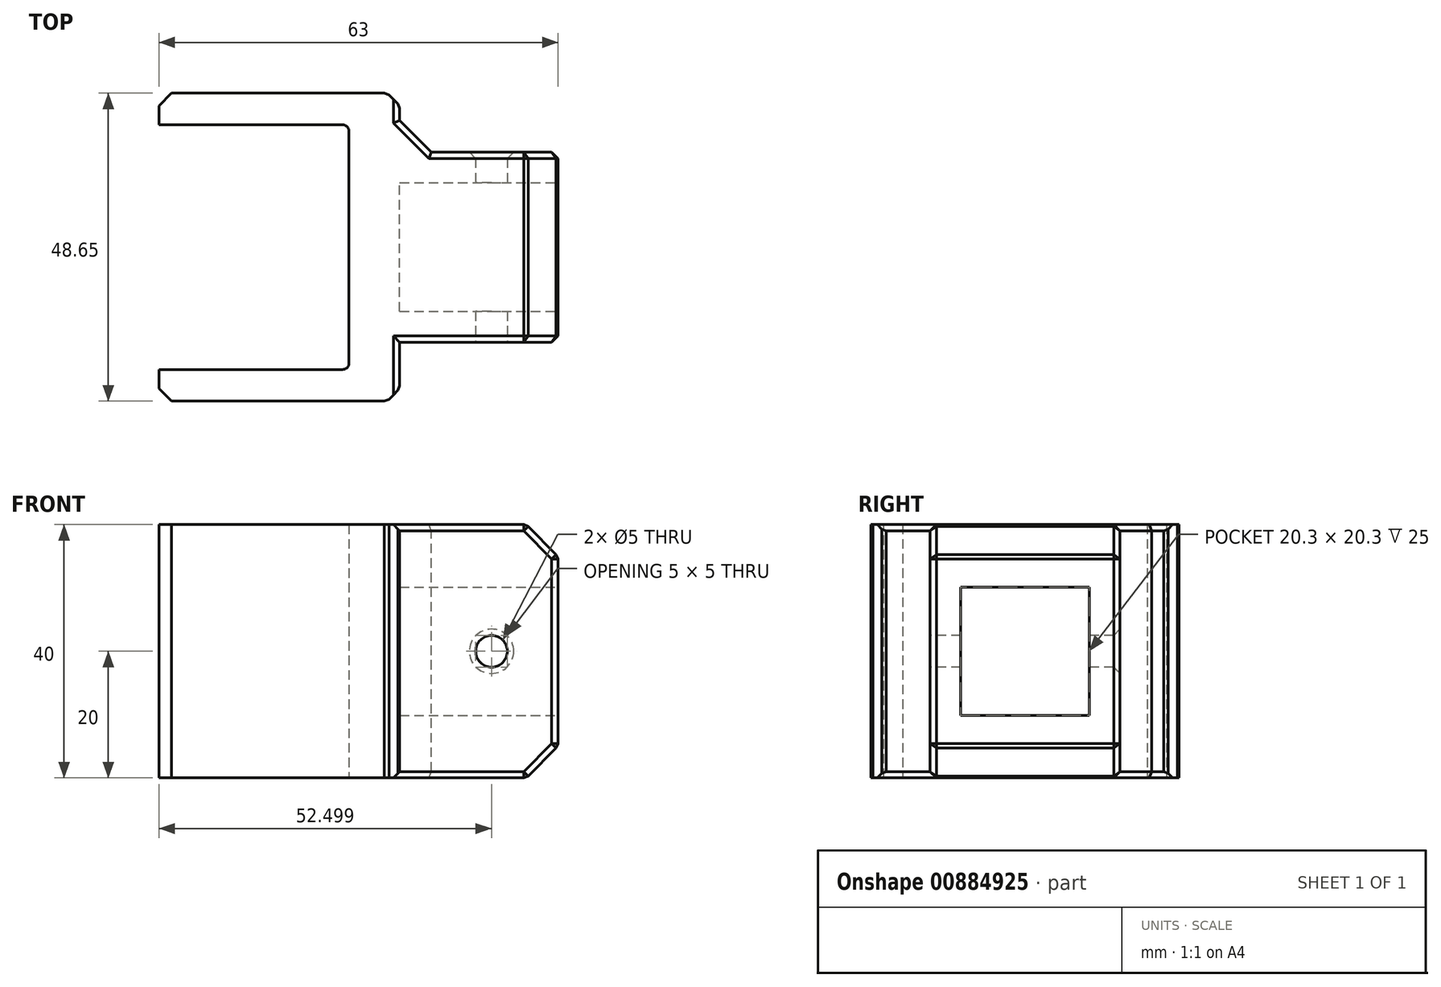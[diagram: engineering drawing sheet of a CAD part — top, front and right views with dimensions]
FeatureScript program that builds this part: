
annotation { "Feature Type Name" : "Feature", "Feature Type Description" : "" }
export const myFeature = defineFeature(function(context is Context, id is Id, definition is map)
    precondition{}
    {
        {
            var Q0;
            Q0=qCreatedBy(makeId("Top.planeOp"),FACE);
            var sketch = newSketch(context, id + "F0", { "sketchPlane" : qUnion([Q0])});
            skLineSegment(sketch, "E0.top", {"start": v(-72.12, -48.29) * mm, "end": v(-110.12, -48.29) * mm});
            skLineSegment(sketch, "E0.right", {"start": v(-110.12, -43.29) * mm, "end": v(-110.12, -48.29) * mm});
            skLineSegment(sketch, "E1.top", {"start": v(-72.12, 0.36) * mm, "end": v(-110.12, 0.36) * mm});
            skLineSegment(sketch, "E1.right", {"start": v(-110.12, -4.64) * mm, "end": v(-110.12, 0.36) * mm});
            skPoint(sketch, "E2", {"position": v(-72.12, 0.36) * mm});
            skLineSegment(sketch, "E3", {"start": v(-72.12, 0.36) * mm, "end": v(-72.12, -48.29) * mm});
            skPoint(sketch, "E4.visualSharp", {"position": v(-47.12, 0.36) * mm});
            skPoint(sketch, "E5.visualSharp", {"position": v(-47.12, -48.29) * mm});
            skPoint(sketch, "E6.end.orphan", {"position": v(-80.12, 0.36) * mm});
            skLineSegment(sketch, "E7.trimOffspring", {"start": v(-80.12, -43.29) * mm, "end": v(-110.12, -43.29) * mm});
            skLineSegment(sketch, "E8.trimOffspring", {"start": v(-80.12, -4.64) * mm, "end": v(-110.12, -4.64) * mm});
            skPoint(sketch, "E0.left.start.orphan", {"position": v(-47.12, -43.29) * mm});
            skPoint(sketch, "E1.left.start.orphan", {"position": v(-47.12, -4.64) * mm});
            skLineSegment(sketch, "E9", {"start": v(-47.12, -8.97) * mm, "end": v(-47.12, -38.97) * mm});
            skLineSegment(sketch, "E10", {"start": v(-80.12, 0.36) * mm, "end": v(-80.12, -48.29) * mm});
            skLineSegment(sketch, "E11.bottom", {"start": v(-47.12, -8.97) * mm, "end": v(-47.12, -8.97) * mm});
            skLineSegment(sketch, "E11.top", {"start": v(-47.12, -38.97) * mm, "end": v(-47.12, -38.97) * mm});
            skPoint(sketch, "E11.middle", {"position": v(-47.12, -23.97) * mm});
            skLineSegment(sketch, "E12", {"start": v(-47.12, -8.97) * mm, "end": v(-72.12, -8.97) * mm});
            skLineSegment(sketch, "E13", {"start": v(-47.12, -38.97) * mm, "end": v(-72.12, -38.97) * mm});
            skSolve(sketch);
        }
        {
            var Q0;
            Q0=makeQuery(id+"F0.imprint","IMPRINT",FACE,{"disambiguationData":[TD([[makeQuery(id+"F0.imprint","IMPRINT",EDGE,{"derivedFrom":sQuery(id+"F0.wireOp",EDGE,"tIqOB3Vk-ss04-YIaf-baA0-UyKqDhGvaing.left")}),1.0]])]});
            var Q1;
            {var subQ4=sQuery(id+"F0.wireOp",EDGE,"E3");Q1=makeQuery(id+"F0.imprint","IMPRINT",FACE,{"disambiguationData":[TD([[makeQuery(id+"F0.imprint","IMPRINT",EDGE,{"derivedFrom":subQ4}),-1.0]])]});}
            var Q2;
            {var subQ0=sQuery(id+"F0.wireOp",EDGE,"E1.right");Q2=makeQuery(id+"F0.imprint","IMPRINT",FACE,{"disambiguationData":[TD([[makeQuery(id+"F0.imprint","IMPRINT",EDGE,{"derivedFrom":subQ0}),-1.0]])]});}
            var Q3;
            {var subQ0=sQuery(id+"F0.wireOp",EDGE,"E0.right");Q3=makeQuery(id+"F0.imprint","IMPRINT",FACE,{"disambiguationData":[TD([[makeQuery(id+"F0.imprint","IMPRINT",EDGE,{"derivedFrom":subQ0}),1.0]])]});}
            extrude(context, id + "F1", {"entities" : qUnion([Q0, Q1, Q2, Q3]), "depth" : 40 * mm, "offsetDistance" : 25 * mm});
        }
        {
            var Q0;
            Q0=makeQuery(id+"F0.imprint","IMPRINT",FACE,{"disambiguationData":[TD([[makeQuery(id+"F0.imprint","IMPRINT",EDGE,{"derivedFrom":sQuery(id+"F0.wireOp",EDGE,"tIqOB3Vk-ss04-YIaf-baA0-UyKqDhGvaing.right")}),-1.0]])]});
            var Q1;
            Q1=makeQuery(id+"F0.imprint","IMPRINT",FACE,{"disambiguationData":[TD([[makeQuery(id+"F0.imprint","IMPRINT",EDGE,{"derivedFrom":sQuery(id+"F0.wireOp",EDGE,"E3")}),1.0]])]});
            extrude(context, id + "F2", {"entities" : qUnion([Q0, Q1]), "operationType" : NewBodyOperationType.ADD, "depth" : 40 * mm, "offsetDistance" : 25 * mm});
        }
        {
            var Q0;
            Q0=makeQuery(id+"F2.opExtrude","SWEPT_FACE",FACE,{"disambiguationData":[OSD([sQuery(id+"F0.wireOp",EDGE,"E9")])]});
            var sketch = newSketch(context, id + "F3", { "sketchPlane" : qUnion([Q0])});
            skLineSegment(sketch, "E14.bottom", {"start": v(-34.12, 9.85) * mm, "end": v(-13.82, 9.85) * mm});
            skLineSegment(sketch, "E14.top", {"start": v(-34.12, 30.15) * mm, "end": v(-13.82, 30.15) * mm});
            skLineSegment(sketch, "E14.left", {"start": v(-34.12, 9.85) * mm, "end": v(-34.12, 30.15) * mm});
            skLineSegment(sketch, "E14.right", {"start": v(-13.82, 9.85) * mm, "end": v(-13.82, 30.15) * mm});
            skPoint(sketch, "E14.middle", {"position": v(-23.97, 20) * mm});
            skPoint(sketch, "E14.middle.positionSnap0", {"position": v(-8.97, 20) * mm});
            skPoint(sketch, "E14.middle.positionSnap1", {"position": v(-23.97, 0) * mm});
            skPoint(sketch, "E14.centerSnap0", {"position": v(-8.97, 20) * mm});
            skPoint(sketch, "E14.centerSnap1", {"position": v(-23.97, 0) * mm});
            skSolve(sketch);
        }
        {
            var Q0;
            Q0=makeQuery(id+"F3.imprint","IMPRINT",FACE,{"disambiguationData":[TD([[makeQuery(id+"F3.imprint","IMPRINT",EDGE,{"derivedFrom":sQuery(id+"F3.wireOp",EDGE,"E14.bottom")}),1.0]])]});
            extrude(context, id + "F4", {"entities" : qUnion([Q0]), "operationType" : NewBodyOperationType.REMOVE, "oppositeDirection" : true, "depth" : 25 * mm, "offsetDistance" : 25 * mm});
        }
        {
            var Q0;
            Q0=makeQuery(id+"F2.opExtrude","SWEPT_EDGE",EDGE,{"disambiguationData":[OSD([sQuery(id+"F0.wireOp",EDGE,"E3"),sQuery(id+"F0.wireOp",EDGE,"E13")])]});
            var Q1;
            Q1=makeQuery(id+"F2.opExtrude","SWEPT_EDGE",EDGE,{"disambiguationData":[OSD([sQuery(id+"F0.wireOp",EDGE,"E3"),sQuery(id+"F0.wireOp",EDGE,"E12")])]});
            var Q2;
            Q2=makeQuery(id+"F2.opExtrude","CAP_EDGE",EDGE,{"disambiguationData":[OSD([sQuery(id+"F0.wireOp",EDGE,"E9")])],"isStart":true});
            var Q3;
            Q3=makeQuery(id+"F2.opExtrude","CAP_EDGE",EDGE,{"disambiguationData":[OSD([sQuery(id+"F0.wireOp",EDGE,"E9")])],"isStart":false});
            chamfer(context, id + "F5", {"entities" : qUnion([Q0, Q1, Q2, Q3]), "width" : 5 * mm, "tangentPropagation" : true});
        }
        {
            var Q0;
            Q0=makeQuery(id+"F1.opExtrude","SWEPT_EDGE",EDGE,{"disambiguationData":[OSD([sQuery(id+"F0.wireOp",EDGE,"E0.top"),sQuery(id+"F0.wireOp",EDGE,"E0.right")])]});
            var Q1;
            Q1=makeQuery(id+"F1.opExtrude","SWEPT_EDGE",EDGE,{"disambiguationData":[OSD([sQuery(id+"F0.wireOp",EDGE,"E1.top"),sQuery(id+"F0.wireOp",EDGE,"E1.right")])]});
            var Q2;
            Q2=makeQuery(id+"F1.opExtrude","SWEPT_EDGE",EDGE,{"disambiguationData":[OSD([sQuery(id+"F0.wireOp",EDGE,"E0.top"),sQuery(id+"F0.wireOp",EDGE,"E3")])]});
            var Q3;
            Q3=makeQuery(id+"F1.opExtrude","SWEPT_EDGE",EDGE,{"disambiguationData":[OSD([sQuery(id+"F0.wireOp",EDGE,"E1.top"),sQuery(id+"F0.wireOp",EDGE,"E3")])]});
            chamfer(context, id + "F6", {"entities" : qUnion([Q0, Q1, Q2, Q3]), "width" : 2 * mm, "tangentPropagation" : true});
        }
        {
            var Q0;
            Q0=makeQuery(id+"F1.opExtrude","SWEPT_EDGE",EDGE,{"disambiguationData":[OSD([sQuery(id+"F0.wireOp",EDGE,"E7.trimOffspring"),sQuery(id+"F0.wireOp",EDGE,"E10")])]});
            var Q1;
            Q1=makeQuery(id+"F1.opExtrude","SWEPT_EDGE",EDGE,{"disambiguationData":[OSD([sQuery(id+"F0.wireOp",EDGE,"E8.trimOffspring"),sQuery(id+"F0.wireOp",EDGE,"E10")])]});
            fillet(context, id + "F7", {"entities" : qUnion([Q0, Q1]), "radius" : 1 * mm, "tangentPropagation" : true, "allowEdgeOverflow" : false});
        }
        {
            var Q0;
            {var subQ0=sQuery(id+"F0.wireOp",EDGE,"E12");var subQ1=sQuery(id+"F0.wireOp",EDGE,"E3");Q0=makeQuery(id+"F5.opChamfer","BLEND_EDGE",EDGE,{"blendedFrom":[makeQuery(id+"F2.opExtrude","SWEPT_EDGE",EDGE,{"disambiguationData":[OSD([subQ1,subQ0])]}),makeQuery(id+"F2.boolean.opBoolean","MERGE",FACE,{"derivedFrom":[makeQuery(id+"F1.opExtrude","CAP_FACE",FACE,{"disambiguationData":[OSD([sQuery(id+"F0.wireOp",EDGE,"E0.top"),sQuery(id+"F0.wireOp",EDGE,"E0.right"),sQuery(id+"F0.wireOp",EDGE,"E1.top"),sQuery(id+"F0.wireOp",EDGE,"E1.right"),subQ1,sQuery(id+"F0.wireOp",EDGE,"E7.trimOffspring"),sQuery(id+"F0.wireOp",EDGE,"E8.trimOffspring"),sQuery(id+"F0.wireOp",EDGE,"E10")])],"isStart":false}),makeQuery(id+"F2.opExtrude","CAP_FACE",FACE,{"disambiguationData":[OSD([subQ1,sQuery(id+"F0.wireOp",EDGE,"E9"),subQ0,sQuery(id+"F0.wireOp",EDGE,"E13")])],"isStart":false})]})],"blendedInto":[makeQuery(id+"F2.boolean.opBoolean","MERGE",FACE,{"derivedFrom":[makeQuery(id+"F1.opExtrude","CAP_FACE",FACE,{"disambiguationData":[OSD([sQuery(id+"F0.wireOp",EDGE,"E0.top"),sQuery(id+"F0.wireOp",EDGE,"E0.right"),sQuery(id+"F0.wireOp",EDGE,"E1.top"),sQuery(id+"F0.wireOp",EDGE,"E1.right"),subQ1,sQuery(id+"F0.wireOp",EDGE,"E7.trimOffspring"),sQuery(id+"F0.wireOp",EDGE,"E8.trimOffspring"),sQuery(id+"F0.wireOp",EDGE,"E10")])],"isStart":false}),makeQuery(id+"F2.opExtrude","CAP_FACE",FACE,{"disambiguationData":[OSD([subQ1,sQuery(id+"F0.wireOp",EDGE,"E9"),subQ0,sQuery(id+"F0.wireOp",EDGE,"E13")])],"isStart":false})]})]});}
            var Q1;
            Q1=makeQuery(id+"F2.opExtrude","CAP_EDGE",EDGE,{"disambiguationData":[OSD([sQuery(id+"F0.wireOp",EDGE,"E12")])],"isStart":false});
            var Q2;
            {var subQ0=sQuery(id+"F0.wireOp",EDGE,"E13");var subQ1=sQuery(id+"F0.wireOp",EDGE,"E3");Q2=makeQuery(id+"F5.opChamfer","BLEND_EDGE",EDGE,{"blendedFrom":[makeQuery(id+"F2.opExtrude","SWEPT_EDGE",EDGE,{"disambiguationData":[OSD([subQ1,subQ0])]}),makeQuery(id+"F2.boolean.opBoolean","MERGE",FACE,{"derivedFrom":[makeQuery(id+"F1.opExtrude","CAP_FACE",FACE,{"disambiguationData":[OSD([sQuery(id+"F0.wireOp",EDGE,"E0.top"),sQuery(id+"F0.wireOp",EDGE,"E0.right"),sQuery(id+"F0.wireOp",EDGE,"E1.top"),sQuery(id+"F0.wireOp",EDGE,"E1.right"),subQ1,sQuery(id+"F0.wireOp",EDGE,"E7.trimOffspring"),sQuery(id+"F0.wireOp",EDGE,"E8.trimOffspring"),sQuery(id+"F0.wireOp",EDGE,"E10")])],"isStart":false}),makeQuery(id+"F2.opExtrude","CAP_FACE",FACE,{"disambiguationData":[OSD([subQ1,sQuery(id+"F0.wireOp",EDGE,"E9"),sQuery(id+"F0.wireOp",EDGE,"E12"),subQ0])],"isStart":false})]})],"blendedInto":[makeQuery(id+"F2.boolean.opBoolean","MERGE",FACE,{"derivedFrom":[makeQuery(id+"F1.opExtrude","CAP_FACE",FACE,{"disambiguationData":[OSD([sQuery(id+"F0.wireOp",EDGE,"E0.top"),sQuery(id+"F0.wireOp",EDGE,"E0.right"),sQuery(id+"F0.wireOp",EDGE,"E1.top"),sQuery(id+"F0.wireOp",EDGE,"E1.right"),subQ1,sQuery(id+"F0.wireOp",EDGE,"E7.trimOffspring"),sQuery(id+"F0.wireOp",EDGE,"E8.trimOffspring"),sQuery(id+"F0.wireOp",EDGE,"E10")])],"isStart":false}),makeQuery(id+"F2.opExtrude","CAP_FACE",FACE,{"disambiguationData":[OSD([subQ1,sQuery(id+"F0.wireOp",EDGE,"E9"),sQuery(id+"F0.wireOp",EDGE,"E12"),subQ0])],"isStart":false})]})]});}
            var Q3;
            Q3=makeQuery(id+"F2.opExtrude","CAP_EDGE",EDGE,{"disambiguationData":[OSD([sQuery(id+"F0.wireOp",EDGE,"E13")])],"isStart":false});
            var Q4;
            {var subQ0=sQuery(id+"F0.wireOp",EDGE,"E13");var subQ1=sQuery(id+"F0.wireOp",EDGE,"E3");Q4=makeQuery(id+"F5.opChamfer","BLEND_EDGE",EDGE,{"blendedFrom":[makeQuery(id+"F2.opExtrude","SWEPT_EDGE",EDGE,{"disambiguationData":[OSD([subQ1,subQ0])]}),makeQuery(id+"F2.boolean.opBoolean","MERGE",FACE,{"derivedFrom":[makeQuery(id+"F1.opExtrude","CAP_FACE",FACE,{"disambiguationData":[OSD([sQuery(id+"F0.wireOp",EDGE,"E0.top"),sQuery(id+"F0.wireOp",EDGE,"E0.right"),sQuery(id+"F0.wireOp",EDGE,"E1.top"),sQuery(id+"F0.wireOp",EDGE,"E1.right"),subQ1,sQuery(id+"F0.wireOp",EDGE,"E7.trimOffspring"),sQuery(id+"F0.wireOp",EDGE,"E8.trimOffspring"),sQuery(id+"F0.wireOp",EDGE,"E10")])],"isStart":true}),makeQuery(id+"F2.opExtrude","CAP_FACE",FACE,{"disambiguationData":[OSD([subQ1,sQuery(id+"F0.wireOp",EDGE,"E9"),sQuery(id+"F0.wireOp",EDGE,"E12"),subQ0])],"isStart":true})]})],"blendedInto":[makeQuery(id+"F2.boolean.opBoolean","MERGE",FACE,{"derivedFrom":[makeQuery(id+"F1.opExtrude","CAP_FACE",FACE,{"disambiguationData":[OSD([sQuery(id+"F0.wireOp",EDGE,"E0.top"),sQuery(id+"F0.wireOp",EDGE,"E0.right"),sQuery(id+"F0.wireOp",EDGE,"E1.top"),sQuery(id+"F0.wireOp",EDGE,"E1.right"),subQ1,sQuery(id+"F0.wireOp",EDGE,"E7.trimOffspring"),sQuery(id+"F0.wireOp",EDGE,"E8.trimOffspring"),sQuery(id+"F0.wireOp",EDGE,"E10")])],"isStart":true}),makeQuery(id+"F2.opExtrude","CAP_FACE",FACE,{"disambiguationData":[OSD([subQ1,sQuery(id+"F0.wireOp",EDGE,"E9"),sQuery(id+"F0.wireOp",EDGE,"E12"),subQ0])],"isStart":true})]})]});}
            var Q5;
            Q5=makeQuery(id+"F2.opExtrude","CAP_EDGE",EDGE,{"disambiguationData":[OSD([sQuery(id+"F0.wireOp",EDGE,"E13")])],"isStart":true});
            var Q6;
            {var subQ0=sQuery(id+"F0.wireOp",EDGE,"E12");var subQ1=sQuery(id+"F0.wireOp",EDGE,"E3");Q6=makeQuery(id+"F5.opChamfer","BLEND_EDGE",EDGE,{"blendedFrom":[makeQuery(id+"F2.opExtrude","SWEPT_EDGE",EDGE,{"disambiguationData":[OSD([subQ1,subQ0])]}),makeQuery(id+"F2.boolean.opBoolean","MERGE",FACE,{"derivedFrom":[makeQuery(id+"F1.opExtrude","CAP_FACE",FACE,{"disambiguationData":[OSD([sQuery(id+"F0.wireOp",EDGE,"E0.top"),sQuery(id+"F0.wireOp",EDGE,"E0.right"),sQuery(id+"F0.wireOp",EDGE,"E1.top"),sQuery(id+"F0.wireOp",EDGE,"E1.right"),subQ1,sQuery(id+"F0.wireOp",EDGE,"E7.trimOffspring"),sQuery(id+"F0.wireOp",EDGE,"E8.trimOffspring"),sQuery(id+"F0.wireOp",EDGE,"E10")])],"isStart":true}),makeQuery(id+"F2.opExtrude","CAP_FACE",FACE,{"disambiguationData":[OSD([subQ1,sQuery(id+"F0.wireOp",EDGE,"E9"),subQ0,sQuery(id+"F0.wireOp",EDGE,"E13")])],"isStart":true})]})],"blendedInto":[makeQuery(id+"F2.boolean.opBoolean","MERGE",FACE,{"derivedFrom":[makeQuery(id+"F1.opExtrude","CAP_FACE",FACE,{"disambiguationData":[OSD([sQuery(id+"F0.wireOp",EDGE,"E0.top"),sQuery(id+"F0.wireOp",EDGE,"E0.right"),sQuery(id+"F0.wireOp",EDGE,"E1.top"),sQuery(id+"F0.wireOp",EDGE,"E1.right"),subQ1,sQuery(id+"F0.wireOp",EDGE,"E7.trimOffspring"),sQuery(id+"F0.wireOp",EDGE,"E8.trimOffspring"),sQuery(id+"F0.wireOp",EDGE,"E10")])],"isStart":true}),makeQuery(id+"F2.opExtrude","CAP_FACE",FACE,{"disambiguationData":[OSD([subQ1,sQuery(id+"F0.wireOp",EDGE,"E9"),subQ0,sQuery(id+"F0.wireOp",EDGE,"E13")])],"isStart":true})]})]});}
            var Q7;
            Q7=makeQuery(id+"F2.opExtrude","CAP_EDGE",EDGE,{"disambiguationData":[OSD([sQuery(id+"F0.wireOp",EDGE,"E12")])],"isStart":true});
            var Q8;
            Q8=makeQuery(id+"F5.opChamfer","BLEND_EDGE",EDGE,{"blendedFrom":[makeQuery(id+"F2.opExtrude","CAP_EDGE",EDGE,{"disambiguationData":[OSD([sQuery(id+"F0.wireOp",EDGE,"E9")])],"isStart":true}),makeQuery(id+"F2.opExtrude","SWEPT_FACE",FACE,{"disambiguationData":[OSD([sQuery(id+"F0.wireOp",EDGE,"E13")])]})],"blendedInto":[makeQuery(id+"F2.opExtrude","SWEPT_FACE",FACE,{"disambiguationData":[OSD([sQuery(id+"F0.wireOp",EDGE,"E13")])]})]});
            var Q9;
            Q9=makeQuery(id+"F5.opChamfer","BLEND_EDGE",EDGE,{"blendedFrom":[makeQuery(id+"F2.opExtrude","CAP_EDGE",EDGE,{"disambiguationData":[OSD([sQuery(id+"F0.wireOp",EDGE,"E9")])],"isStart":false}),makeQuery(id+"F2.opExtrude","SWEPT_FACE",FACE,{"disambiguationData":[OSD([sQuery(id+"F0.wireOp",EDGE,"E13")])]})],"blendedInto":[makeQuery(id+"F2.opExtrude","SWEPT_FACE",FACE,{"disambiguationData":[OSD([sQuery(id+"F0.wireOp",EDGE,"E13")])]})]});
            var Q10;
            Q10=makeQuery(id+"F2.opExtrude","SWEPT_EDGE",EDGE,{"disambiguationData":[OSD([sQuery(id+"F0.wireOp",EDGE,"E9"),sQuery(id+"F0.wireOp",EDGE,"E13")])]});
            var Q11;
            Q11=makeQuery(id+"F2.opExtrude","SWEPT_EDGE",EDGE,{"disambiguationData":[OSD([sQuery(id+"F0.wireOp",EDGE,"E9"),sQuery(id+"F0.wireOp",EDGE,"E12")])]});
            var Q12;
            Q12=makeQuery(id+"F5.opChamfer","BLEND_EDGE",EDGE,{"blendedFrom":[makeQuery(id+"F2.opExtrude","CAP_EDGE",EDGE,{"disambiguationData":[OSD([sQuery(id+"F0.wireOp",EDGE,"E9")])],"isStart":false}),makeQuery(id+"F2.opExtrude","SWEPT_FACE",FACE,{"disambiguationData":[OSD([sQuery(id+"F0.wireOp",EDGE,"E12")])]})],"blendedInto":[makeQuery(id+"F2.opExtrude","SWEPT_FACE",FACE,{"disambiguationData":[OSD([sQuery(id+"F0.wireOp",EDGE,"E12")])]})]});
            var Q13;
            Q13=makeQuery(id+"F5.opChamfer","BLEND_EDGE",EDGE,{"blendedFrom":[makeQuery(id+"F2.opExtrude","CAP_EDGE",EDGE,{"disambiguationData":[OSD([sQuery(id+"F0.wireOp",EDGE,"E9")])],"isStart":true}),makeQuery(id+"F2.opExtrude","SWEPT_FACE",FACE,{"disambiguationData":[OSD([sQuery(id+"F0.wireOp",EDGE,"E12")])]})],"blendedInto":[makeQuery(id+"F2.opExtrude","SWEPT_FACE",FACE,{"disambiguationData":[OSD([sQuery(id+"F0.wireOp",EDGE,"E12")])]})]});
            var Q14;
            {var subQ0=sQuery(id+"F0.wireOp",EDGE,"E9");var subQ1=sQuery(id+"F0.wireOp",EDGE,"E3");Q14=makeQuery(id+"F5.opChamfer","BLEND_EDGE",EDGE,{"blendedFrom":[makeQuery(id+"F2.opExtrude","CAP_EDGE",EDGE,{"disambiguationData":[OSD([subQ0])],"isStart":true}),makeQuery(id+"F2.boolean.opBoolean","MERGE",FACE,{"derivedFrom":[makeQuery(id+"F1.opExtrude","CAP_FACE",FACE,{"disambiguationData":[OSD([sQuery(id+"F0.wireOp",EDGE,"E0.top"),sQuery(id+"F0.wireOp",EDGE,"E0.right"),sQuery(id+"F0.wireOp",EDGE,"E1.top"),sQuery(id+"F0.wireOp",EDGE,"E1.right"),subQ1,sQuery(id+"F0.wireOp",EDGE,"E7.trimOffspring"),sQuery(id+"F0.wireOp",EDGE,"E8.trimOffspring"),sQuery(id+"F0.wireOp",EDGE,"E10")])],"isStart":true}),makeQuery(id+"F2.opExtrude","CAP_FACE",FACE,{"disambiguationData":[OSD([subQ1,subQ0,sQuery(id+"F0.wireOp",EDGE,"E12"),sQuery(id+"F0.wireOp",EDGE,"E13")])],"isStart":true})]})],"blendedInto":[makeQuery(id+"F2.boolean.opBoolean","MERGE",FACE,{"derivedFrom":[makeQuery(id+"F1.opExtrude","CAP_FACE",FACE,{"disambiguationData":[OSD([sQuery(id+"F0.wireOp",EDGE,"E0.top"),sQuery(id+"F0.wireOp",EDGE,"E0.right"),sQuery(id+"F0.wireOp",EDGE,"E1.top"),sQuery(id+"F0.wireOp",EDGE,"E1.right"),subQ1,sQuery(id+"F0.wireOp",EDGE,"E7.trimOffspring"),sQuery(id+"F0.wireOp",EDGE,"E8.trimOffspring"),sQuery(id+"F0.wireOp",EDGE,"E10")])],"isStart":true}),makeQuery(id+"F2.opExtrude","CAP_FACE",FACE,{"disambiguationData":[OSD([subQ1,subQ0,sQuery(id+"F0.wireOp",EDGE,"E12"),sQuery(id+"F0.wireOp",EDGE,"E13")])],"isStart":true})]})]});}
            var Q15;
            {var subQ0=sQuery(id+"F0.wireOp",EDGE,"E9");var subQ1=sQuery(id+"F0.wireOp",EDGE,"E3");Q15=makeQuery(id+"F5.opChamfer","BLEND_EDGE",EDGE,{"blendedFrom":[makeQuery(id+"F2.opExtrude","CAP_EDGE",EDGE,{"disambiguationData":[OSD([subQ0])],"isStart":false}),makeQuery(id+"F2.boolean.opBoolean","MERGE",FACE,{"derivedFrom":[makeQuery(id+"F1.opExtrude","CAP_FACE",FACE,{"disambiguationData":[OSD([sQuery(id+"F0.wireOp",EDGE,"E0.top"),sQuery(id+"F0.wireOp",EDGE,"E0.right"),sQuery(id+"F0.wireOp",EDGE,"E1.top"),sQuery(id+"F0.wireOp",EDGE,"E1.right"),subQ1,sQuery(id+"F0.wireOp",EDGE,"E7.trimOffspring"),sQuery(id+"F0.wireOp",EDGE,"E8.trimOffspring"),sQuery(id+"F0.wireOp",EDGE,"E10")])],"isStart":false}),makeQuery(id+"F2.opExtrude","CAP_FACE",FACE,{"disambiguationData":[OSD([subQ1,subQ0,sQuery(id+"F0.wireOp",EDGE,"E12"),sQuery(id+"F0.wireOp",EDGE,"E13")])],"isStart":false})]})],"blendedInto":[makeQuery(id+"F2.boolean.opBoolean","MERGE",FACE,{"derivedFrom":[makeQuery(id+"F1.opExtrude","CAP_FACE",FACE,{"disambiguationData":[OSD([sQuery(id+"F0.wireOp",EDGE,"E0.top"),sQuery(id+"F0.wireOp",EDGE,"E0.right"),sQuery(id+"F0.wireOp",EDGE,"E1.top"),sQuery(id+"F0.wireOp",EDGE,"E1.right"),subQ1,sQuery(id+"F0.wireOp",EDGE,"E7.trimOffspring"),sQuery(id+"F0.wireOp",EDGE,"E8.trimOffspring"),sQuery(id+"F0.wireOp",EDGE,"E10")])],"isStart":false}),makeQuery(id+"F2.opExtrude","CAP_FACE",FACE,{"disambiguationData":[OSD([subQ1,subQ0,sQuery(id+"F0.wireOp",EDGE,"E12"),sQuery(id+"F0.wireOp",EDGE,"E13")])],"isStart":false})]})]});}
            var Q16;
            {var subQ0=sQuery(id+"F0.wireOp",EDGE,"E9");Q16=makeQuery(id+"F5.opChamfer","BLEND_EDGE",EDGE,{"blendedFrom":[makeQuery(id+"F2.opExtrude","CAP_EDGE",EDGE,{"disambiguationData":[OSD([subQ0])],"isStart":false}),makeQuery(id+"F2.opExtrude","SWEPT_FACE",FACE,{"disambiguationData":[OSD([subQ0])]})],"blendedInto":[makeQuery(id+"F2.opExtrude","SWEPT_FACE",FACE,{"disambiguationData":[OSD([subQ0])]})]});}
            var Q17;
            {var subQ0=sQuery(id+"F0.wireOp",EDGE,"E9");Q17=makeQuery(id+"F5.opChamfer","BLEND_EDGE",EDGE,{"blendedFrom":[makeQuery(id+"F2.opExtrude","CAP_EDGE",EDGE,{"disambiguationData":[OSD([subQ0])],"isStart":true}),makeQuery(id+"F2.opExtrude","SWEPT_FACE",FACE,{"disambiguationData":[OSD([subQ0])]})],"blendedInto":[makeQuery(id+"F2.opExtrude","SWEPT_FACE",FACE,{"disambiguationData":[OSD([subQ0])]})]});}
            var Q18;
            {var subQ1=sQuery(id+"F0.wireOp",EDGE,"E3");var subQ2=sQuery(id+"F0.wireOp",EDGE,"E0.top");Q18=makeQuery(id+"F2.boolean.opBoolean","SPLIT",EDGE,{"disambiguationData":[TD([makeQuery(id+"F1.opExtrude","SWEPT_FACE",FACE,{"disambiguationData":[OSD([subQ2])]})])],"derivedFrom":makeQuery(id+"F1.opExtrude","CAP_EDGE",EDGE,{"disambiguationData":[OSD([subQ1])],"isStart":false})});}
            var Q19;
            {var subQ1=sQuery(id+"F0.wireOp",EDGE,"E3");var subQ2=sQuery(id+"F0.wireOp",EDGE,"E0.top");Q19=makeQuery(id+"F2.boolean.opBoolean","SPLIT",EDGE,{"disambiguationData":[TD([makeQuery(id+"F1.opExtrude","SWEPT_FACE",FACE,{"disambiguationData":[OSD([subQ2])]})])],"derivedFrom":makeQuery(id+"F1.opExtrude","CAP_EDGE",EDGE,{"disambiguationData":[OSD([subQ1])],"isStart":true})});}
            var Q20;
            {var subQ1=sQuery(id+"F0.wireOp",EDGE,"E3");var subQ2=sQuery(id+"F0.wireOp",EDGE,"E1.top");Q20=makeQuery(id+"F2.boolean.opBoolean","SPLIT",EDGE,{"disambiguationData":[TD([makeQuery(id+"F1.opExtrude","SWEPT_FACE",FACE,{"disambiguationData":[OSD([subQ2])]})])],"derivedFrom":makeQuery(id+"F1.opExtrude","CAP_EDGE",EDGE,{"disambiguationData":[OSD([subQ1])],"isStart":false})});}
            var Q21;
            {var subQ1=sQuery(id+"F0.wireOp",EDGE,"E3");var subQ2=sQuery(id+"F0.wireOp",EDGE,"E1.top");Q21=makeQuery(id+"F2.boolean.opBoolean","SPLIT",EDGE,{"disambiguationData":[TD([makeQuery(id+"F1.opExtrude","SWEPT_FACE",FACE,{"disambiguationData":[OSD([subQ2])]})])],"derivedFrom":makeQuery(id+"F1.opExtrude","CAP_EDGE",EDGE,{"disambiguationData":[OSD([subQ1])],"isStart":true})});}
            var Q22;
            {var subQ3=sQuery(id+"F0.wireOp",EDGE,"E3");var subQ10=sQuery(id+"F0.wireOp",EDGE,"E0.top");Q22=makeQuery(id+"F6.opChamfer","BLEND_EDGE",EDGE,{"blendedFrom":[makeQuery(id+"F1.opExtrude","SWEPT_EDGE",EDGE,{"disambiguationData":[OSD([subQ10,subQ3])]}),makeQuery(id+"F2.boolean.opBoolean","SPLIT",FACE,{"disambiguationData":[TD([makeQuery(id+"F1.opExtrude","SWEPT_FACE",FACE,{"disambiguationData":[OSD([subQ10])]})])],"derivedFrom":makeQuery(id+"F1.opExtrude","SWEPT_FACE",FACE,{"disambiguationData":[OSD([subQ3])]})})],"blendedInto":[makeQuery(id+"F2.boolean.opBoolean","SPLIT",FACE,{"disambiguationData":[TD([makeQuery(id+"F1.opExtrude","SWEPT_FACE",FACE,{"disambiguationData":[OSD([subQ10])]})])],"derivedFrom":makeQuery(id+"F1.opExtrude","SWEPT_FACE",FACE,{"disambiguationData":[OSD([subQ3])]})})]});}
            var Q23;
            {var subQ0=sQuery(id+"F0.wireOp",EDGE,"E1.top");var subQ4=sQuery(id+"F0.wireOp",EDGE,"E3");Q23=makeQuery(id+"F6.opChamfer","BLEND_EDGE",EDGE,{"blendedFrom":[makeQuery(id+"F1.opExtrude","SWEPT_EDGE",EDGE,{"disambiguationData":[OSD([subQ0,subQ4])]}),makeQuery(id+"F2.boolean.opBoolean","SPLIT",FACE,{"disambiguationData":[TD([makeQuery(id+"F1.opExtrude","SWEPT_FACE",FACE,{"disambiguationData":[OSD([subQ0])]})])],"derivedFrom":makeQuery(id+"F1.opExtrude","SWEPT_FACE",FACE,{"disambiguationData":[OSD([subQ4])]})})],"blendedInto":[makeQuery(id+"F2.boolean.opBoolean","SPLIT",FACE,{"disambiguationData":[TD([makeQuery(id+"F1.opExtrude","SWEPT_FACE",FACE,{"disambiguationData":[OSD([subQ0])]})])],"derivedFrom":makeQuery(id+"F1.opExtrude","SWEPT_FACE",FACE,{"disambiguationData":[OSD([subQ4])]})})]});}
            var Q24;
            {var subQ0=sQuery(id+"F0.wireOp",EDGE,"E1.top");Q24=makeQuery(id+"F6.opChamfer","BLEND_EDGE",EDGE,{"blendedFrom":[makeQuery(id+"F1.opExtrude","SWEPT_EDGE",EDGE,{"disambiguationData":[OSD([subQ0,sQuery(id+"F0.wireOp",EDGE,"E3")])]}),makeQuery(id+"F1.opExtrude","SWEPT_FACE",FACE,{"disambiguationData":[OSD([subQ0])]})],"blendedInto":[makeQuery(id+"F1.opExtrude","SWEPT_FACE",FACE,{"disambiguationData":[OSD([subQ0])]})]});}
            var Q25;
            {var subQ0=sQuery(id+"F0.wireOp",EDGE,"E0.top");Q25=makeQuery(id+"F6.opChamfer","BLEND_EDGE",EDGE,{"blendedFrom":[makeQuery(id+"F1.opExtrude","SWEPT_EDGE",EDGE,{"disambiguationData":[OSD([subQ0,sQuery(id+"F0.wireOp",EDGE,"E3")])]}),makeQuery(id+"F1.opExtrude","SWEPT_FACE",FACE,{"disambiguationData":[OSD([subQ0])]})],"blendedInto":[makeQuery(id+"F1.opExtrude","SWEPT_FACE",FACE,{"disambiguationData":[OSD([subQ0])]})]});}
            chamfer(context, id + "F8", {"entities" : qUnion([Q0, Q1, Q2, Q3, Q4, Q5, Q6, Q7, Q8, Q9, Q10, Q11, Q12, Q13, Q14, Q15, Q16, Q17, Q18, Q19, Q20, Q21, Q22, Q23, Q24, Q25]), "width" : 1 * mm, "tangentPropagation" : true});
        }
        {
            var Q0;
            Q0=makeQuery(id+"F2.opExtrude","SWEPT_FACE",FACE,{"disambiguationData":[OSD([sQuery(id+"F0.wireOp",EDGE,"E13")])]});
            var sketch = newSketch(context, id + "F9", { "sketchPlane" : qUnion([Q0])});
            skLineSegment(sketch, "E15", {"start": v(-67.12, 20) * mm, "end": v(-48.12, 20) * mm});
            skCircle(sketch, "E16", {"center": v(-57.62, 20) * mm, "radius": 2.5 * mm});
            skSolve(sketch);
        }
        {
            var Q0;
            {var subQ0=sQuery(id+"F9.wireOp",EDGE,"E16");var subQ1=sQuery(id+"F9.wireOp",EDGE,"E15");var subQ2=makeQuery(id+"F9.imprint","INTERSECT",VERTEX,{"disambiguationData":[OD(0.0)],"derivedFrom":[subQ1,subQ0]});Q0=makeQuery(id+"F9.imprint","IMPRINT",FACE,{"disambiguationData":[TD([[makeQuery(id+"F9.imprint","IMPRINT",EDGE,{"disambiguationData":[TD([[subQ2,-1.0]])],"derivedFrom":subQ1}),1.0]])]});}
            var Q1;
            {var subQ0=sQuery(id+"F9.wireOp",EDGE,"E16");var subQ1=sQuery(id+"F9.wireOp",EDGE,"E15");var subQ2=makeQuery(id+"F9.imprint","INTERSECT",VERTEX,{"disambiguationData":[OD(0.0)],"derivedFrom":[subQ1,subQ0]});Q1=makeQuery(id+"F9.imprint","IMPRINT",FACE,{"disambiguationData":[TD([[makeQuery(id+"F9.imprint","IMPRINT",EDGE,{"disambiguationData":[TD([[subQ2,-1.0]])],"derivedFrom":subQ1}),-1.0]])]});}
            extrude(context, id + "F10", {"entities" : qUnion([Q0, Q1]), "operationType" : NewBodyOperationType.REMOVE, "oppositeDirection" : true, "depth" : 50 * mm, "offsetDistance" : 25 * mm});
        }
        {
            var Q0;
            Q0=makeQuery(id+"F10.boolean.opBoolean","INTERSECT",EDGE,{"derivedFrom":[makeQuery(id+"F2.opExtrude","SWEPT_FACE",FACE,{"disambiguationData":[OSD([sQuery(id+"F0.wireOp",EDGE,"E12")])]}),makeQuery(id+"F10.opExtrude","SWEPT_FACE",FACE,{"disambiguationData":[OSD([sQuery(id+"F9.wireOp",EDGE,"E16")])]})]});
            var Q1;
            Q1=makeQuery(id+"F10.boolean.opBoolean","COPY",EDGE,{"derivedFrom":makeQuery(id+"F10.opExtrude","CAP_EDGE",EDGE,{"disambiguationData":[OSD([sQuery(id+"F9.wireOp",EDGE,"E16")])],"isStart":true})});
            chamfer(context, id + "F11", {"entities" : qUnion([Q0, Q1]), "width" : 1 * mm, "tangentPropagation" : true});
        }
    });
